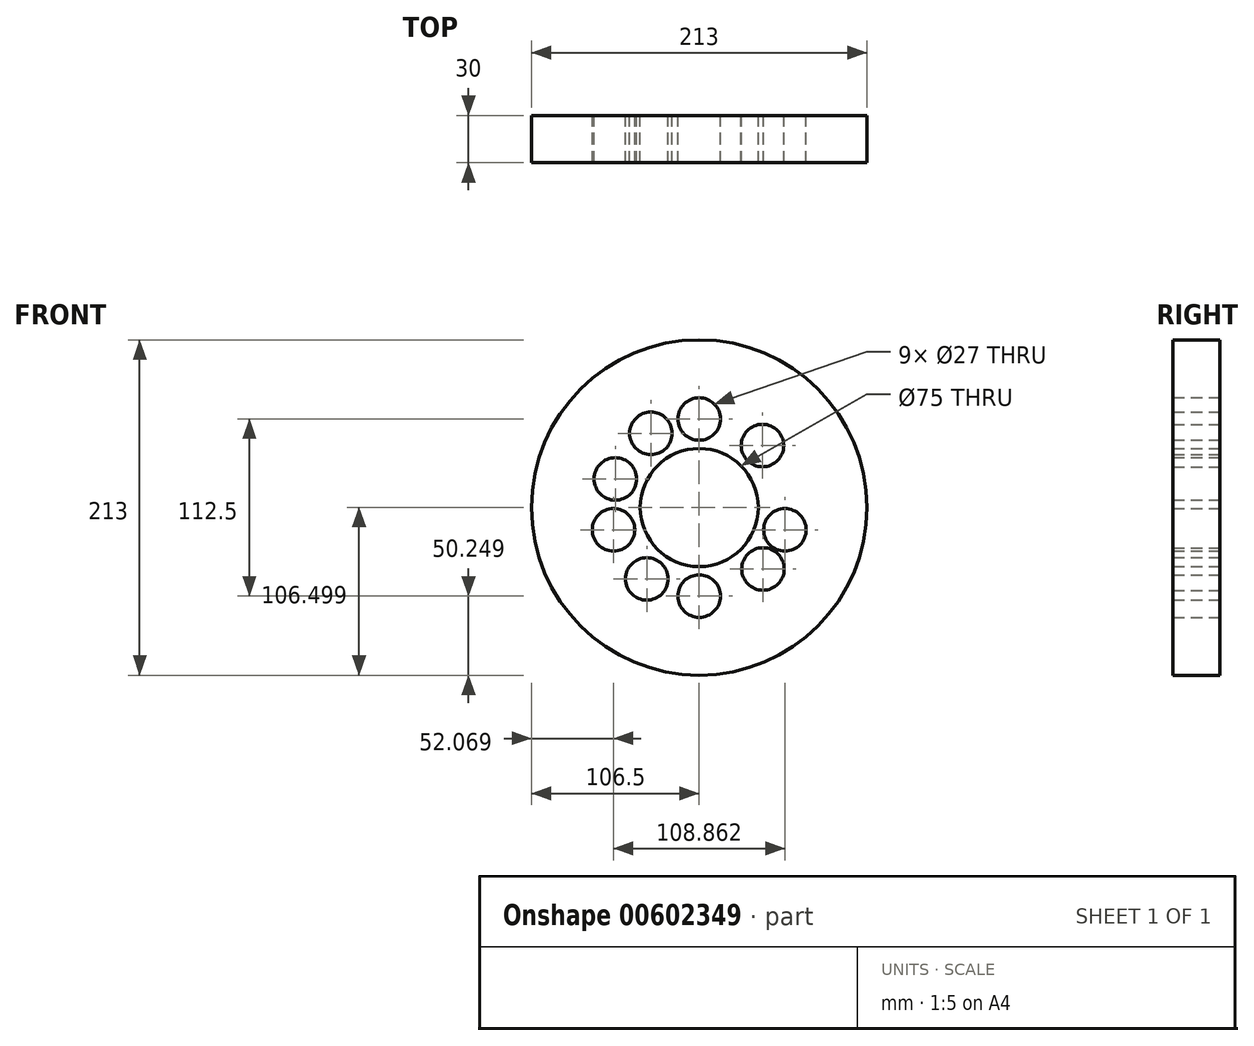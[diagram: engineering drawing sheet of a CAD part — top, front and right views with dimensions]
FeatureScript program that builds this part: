
annotation { "Feature Type Name" : "Feature", "Feature Type Description" : "" }
export const myFeature = defineFeature(function(context is Context, id is Id, definition is map)
    precondition{}
    {
        {
            var Q0;
            Q0=qCreatedBy(makeId("Front.planeOp"),FACE);
            var sketch = newSketch(context, id + "F0", { "sketchPlane" : qUnion([Q0])});
            skCircle(sketch, "E0", {"center": v(-61.07, 14.19) * mm, "radius": 106.5 * mm});
            skCircle(sketch, "E1", {"center": v(-61.07, 14.19) * mm, "radius": 75 * mm});
            skCircle(sketch, "E2", {"center": v(-61.07, 14.19) * mm, "radius": 37.5 * mm});
            skCircle(sketch, "E3", {"center": v(-61.07, 14.19) * mm, "radius": 32.5 * mm});
            skCircle(sketch, "E4", {"center": v(-61.07, 70.44) * mm, "radius": 13.5 * mm});
            skCircle(sketch, "E5", {"center": v(-91.75, 61.34) * mm, "radius": 13.5 * mm});
            skCircle(sketch, "E6", {"center": v(-20.88, 53.55) * mm, "radius": 13.5 * mm});
            skCircle(sketch, "E7", {"center": v(-114.3, 32.35) * mm, "radius": 13.5 * mm});
            skCircle(sketch, "E8", {"center": v(-115.5, 0) * mm, "radius": 13.5 * mm});
            skCircle(sketch, "E9", {"center": v(-94.35, -31.16) * mm, "radius": 13.5 * mm});
            skCircle(sketch, "E10", {"center": v(-61.07, -42.06) * mm, "radius": 13.5 * mm});
            skCircle(sketch, "E11", {"center": v(-20.6, -24.87) * mm, "radius": 13.5 * mm});
            skCircle(sketch, "E12", {"center": v(-6.64, 0) * mm, "radius": 13.5 * mm});
            skSolve(sketch);
        }
        {
            var Q0;
            Q0 = qSketchRegion(id + "F0", true);
            var Q1;
            Q1=makeQuery(id+"F0.imprint","IMPRINT",FACE,{"disambiguationData":[TD([[makeQuery(id+"F0.imprint","IMPRINT",EDGE,{"derivedFrom":sQuery(id+"F0.wireOp",EDGE,"E1")}),1.0]])]});
            extrude(context, id + "F1", {"entities" : qUnion([Q0, Q1]), "depth" : 30 * mm, "offsetDistance" : 25 * mm});
        }
    });
